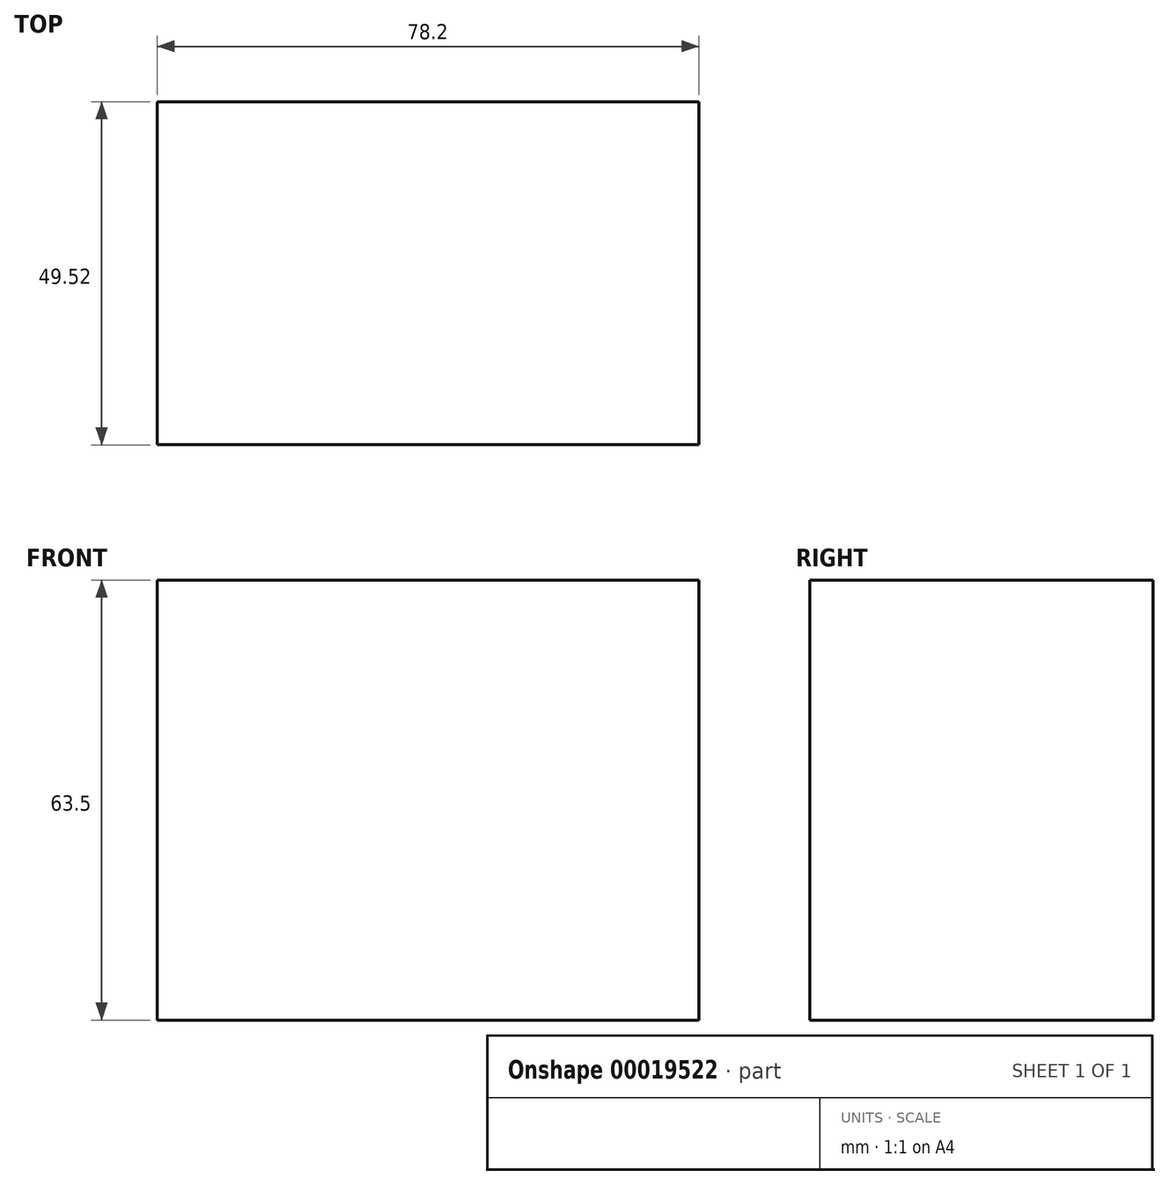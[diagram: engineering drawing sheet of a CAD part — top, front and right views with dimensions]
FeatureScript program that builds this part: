
annotation { "Feature Type Name" : "Feature", "Feature Type Description" : "" }
export const myFeature = defineFeature(function(context is Context, id is Id, definition is map)
    precondition{}
    {
        {
            var Q0;
            Q0=qCreatedBy(makeId("Top.planeOp"),FACE);
            var sketch = newSketch(context, id + "F0", { "sketchPlane" : qUnion([Q0])});
            skLineSegment(sketch, "E0.rect.bottom", {"start": v(39.1, 24.76) * mm, "end": v(-39.1, 24.76) * mm});
            skLineSegment(sketch, "E0.rect.top", {"start": v(39.1, -24.76) * mm, "end": v(-39.1, -24.76) * mm});
            skLineSegment(sketch, "E0.rect.left", {"start": v(39.1, 24.76) * mm, "end": v(39.1, -24.76) * mm});
            skLineSegment(sketch, "E0.rect.right", {"start": v(-39.1, 24.76) * mm, "end": v(-39.1, -24.76) * mm});
            skPoint(sketch, "E0.rect.middle", {"position": v(0, 0) * mm});
            skSolve(sketch);
        }
        {
            var Q0;
            Q0 = qSketchRegion(id + "F0", true);
            extrude(context, id + "F1", {"entities" : qUnion([Q0]), "depth" : 63.5 * mm});
        }
    });
